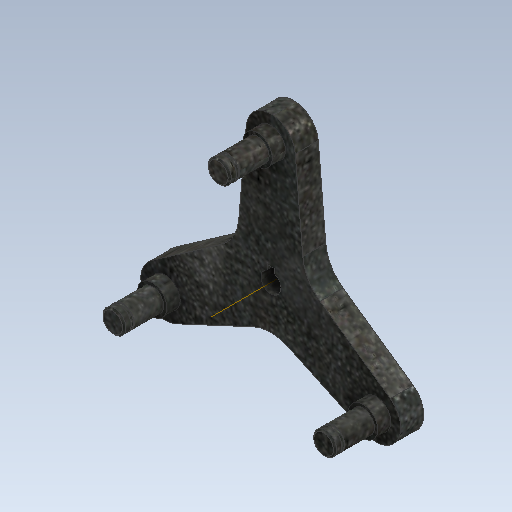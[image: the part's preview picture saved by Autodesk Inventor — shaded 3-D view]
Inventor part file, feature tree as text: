
AUTODESK INVENTOR PART (.ipt)
format: ipt  version: 2021 (Build 250183000, 183)  size: 322,560 bytes
history: native  units: mm
features: extrude x4, sketch x4, revolve x2, projected_geometry x2, other x1, chamfer x1, pattern_circular x1
ambient origin geometry x8: Origin, YZ Plane, XZ Plane, XY Plane, X Axis, Y Axis, Z Axis, Center Point
bodies: Solid1 (feature_tree)
feature tree (15):
  revolve  "Revolution1"  Angle=90.0deg
  extrude  "Extrusion1"  Depth=15.0mm
  sketch  "Sketch4"  dims[d4=45.0mm d6=15.0mm]
  extrude  "Extrusion2"  TaperAngle=120.0deg  [1 undecoded]
  extrude  "Extrusion4"  TaperAngle=60.0deg  [1 undecoded]
  other  "Work Axis2"
  revolve  "Revolution2"  [1 undecoded]
  chamfer  "Chamfer1"  Distance=25.0mm
  pattern_circular  "Circular Pattern1"  [2 undecoded]
  extrude  "Extrusion5"  TaperAngle=0.0deg  [1 undecoded]
  sketch  "Sketch2"  dims[d1=23.0mm d2=90.0deg]
  projected_geometry  "Projected Loop1"
  sketch  "Sketch6"  dims[d7=120.0deg d8=120.0deg]
  projected_geometry  "Projected Loop2"
  sketch  "Sketch7"  dims[d9=60.0deg d10=60.0deg d11=37.075mm d12=25.0mm d13=0.872665mm d14=0.0mm d15=0.0mm d16=30.0mm d17=360.0deg d20=9.0mm d21=16.0mm d22=0.0mm d23=7.0mm d26=12.0mm d27=0.0mm d29=9.0mm d30=90.0deg d31=0.5mm d32=2.0mm d33=45.0deg d34=6.8mm d35=0.9mm d36=3.0mm d37=2.0mm d38=2.2mm d39=2.0mm d40=0.0mm d41=0.0mm]
note: 6 required parameter values undecoded (feature->parameter linkage not recoverable at this tier; creation-order binding heuristic only, values carry confidence <= 0.55)